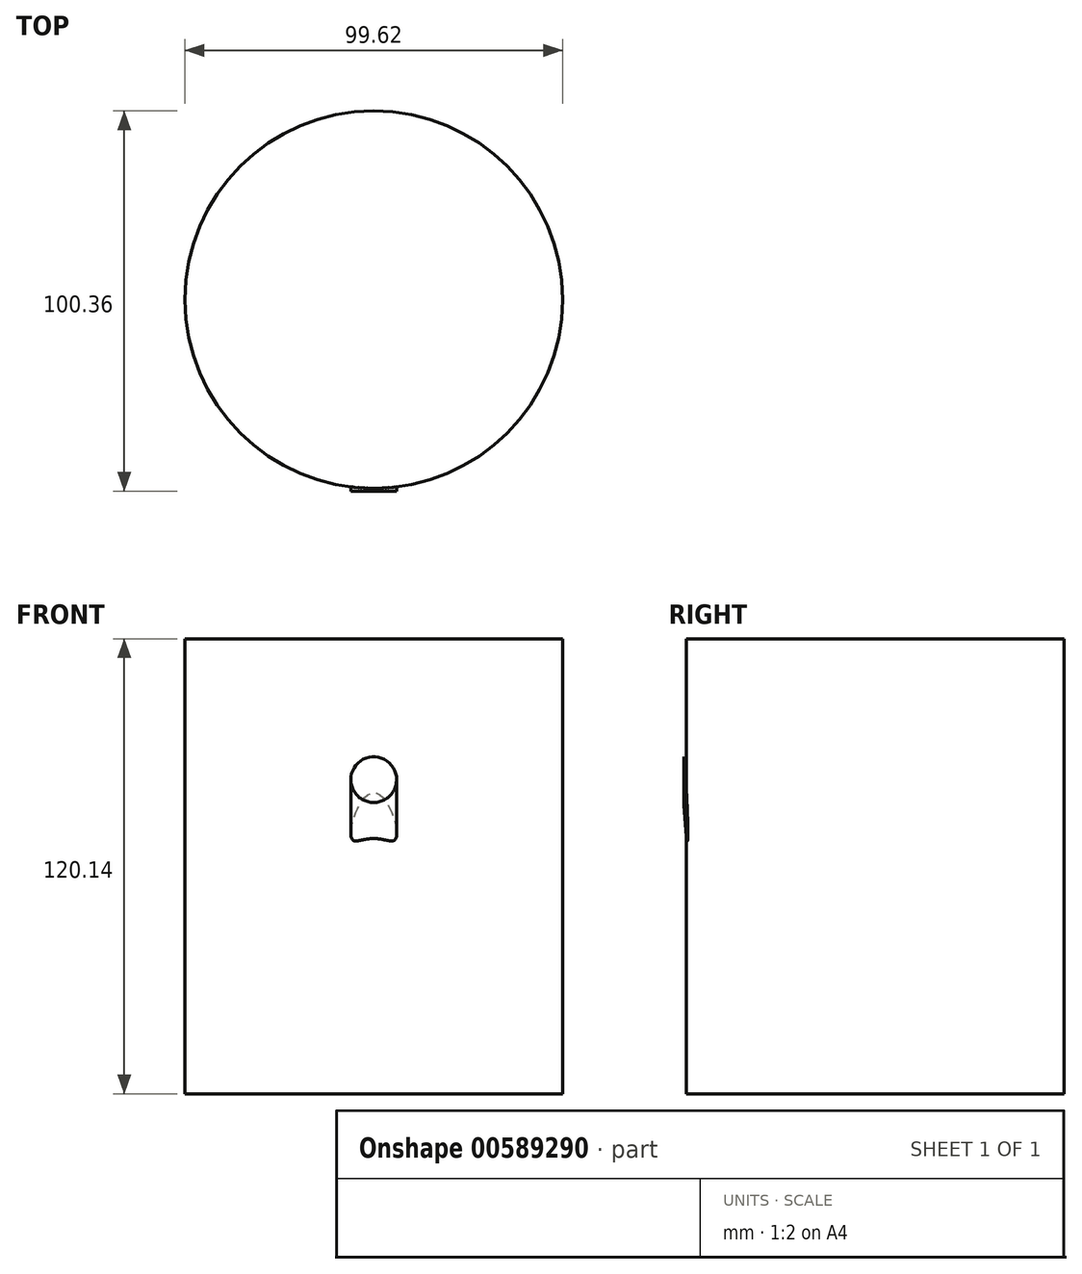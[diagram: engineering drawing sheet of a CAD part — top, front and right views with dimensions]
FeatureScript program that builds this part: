
annotation { "Feature Type Name" : "Feature", "Feature Type Description" : "" }
export const myFeature = defineFeature(function(context is Context, id is Id, definition is map)
    precondition{}
    {
        {
            var Q0;
            Q0=qCreatedBy(makeId("Top.planeOp"),FACE);
            var sketch = newSketch(context, id + "F0", { "sketchPlane" : qUnion([Q0])});
            skCircle(sketch, "E0", {"center": v(0, 0) * mm, "radius": 49.81 * mm});
            skSolve(sketch);
        }
        {
            var Q0;
            Q0=makeQuery(id+"F0.imprint","IMPRINT",FACE,{"disambiguationData":[TD([[makeQuery(id+"F0.imprint","IMPRINT",EDGE,{"derivedFrom":sQuery(id+"F0.wireOp",EDGE,"E0")}),1.0]])]});
            extrude(context, id + "F1", {"entities" : qUnion([Q0]), "depth" : 120.14 * mm, "offsetDistance" : 25.4 * mm});
        }
        {
            var Q0;
            Q0=qCreatedBy(makeId("Right.planeOp"),FACE);
            var sketch = newSketch(context, id + "F2", { "sketchPlane" : qUnion([Q0])});
            skLineSegment(sketch, "E1", {"start": v(-45.25, 88.4) * mm, "end": v(-39.9, 19.01) * mm});
            skSolve(sketch);
        }
        {
            var Q0;
            Q0=qCreatedBy(makeId("Front.planeOp"),FACE);
            cPlane(context, id + "F3", {"entities" : qUnion([Q0]), "cplaneType" : CPlaneType.OFFSET, "offset" : 50.55 * mm, "width" : 152.4 * mm, "height" : 152.4 * mm});
        }
        {
            var Q0;
            Q0=qCreatedBy(id+"F3.planeOp",FACE);
            var sketch = newSketch(context, id + "F4", { "sketchPlane" : qUnion([Q0])});
            skCircle(sketch, "E2", {"center": v(0, 82.95) * mm, "radius": 6.04 * mm});
            skSolve(sketch);
        }
        {
            var Q0;
            Q0 = qSketchRegion(id + "F4", true);
            var Q1;
            Q1=sQuery(id+"F2.wireOp",EDGE,"E1");
            sweep(context, id + "F5", {"operationType" : NewBodyOperationType.ADD, "profiles" : qUnion([Q0]), "path" : qUnion([Q1])});
        }
    });
